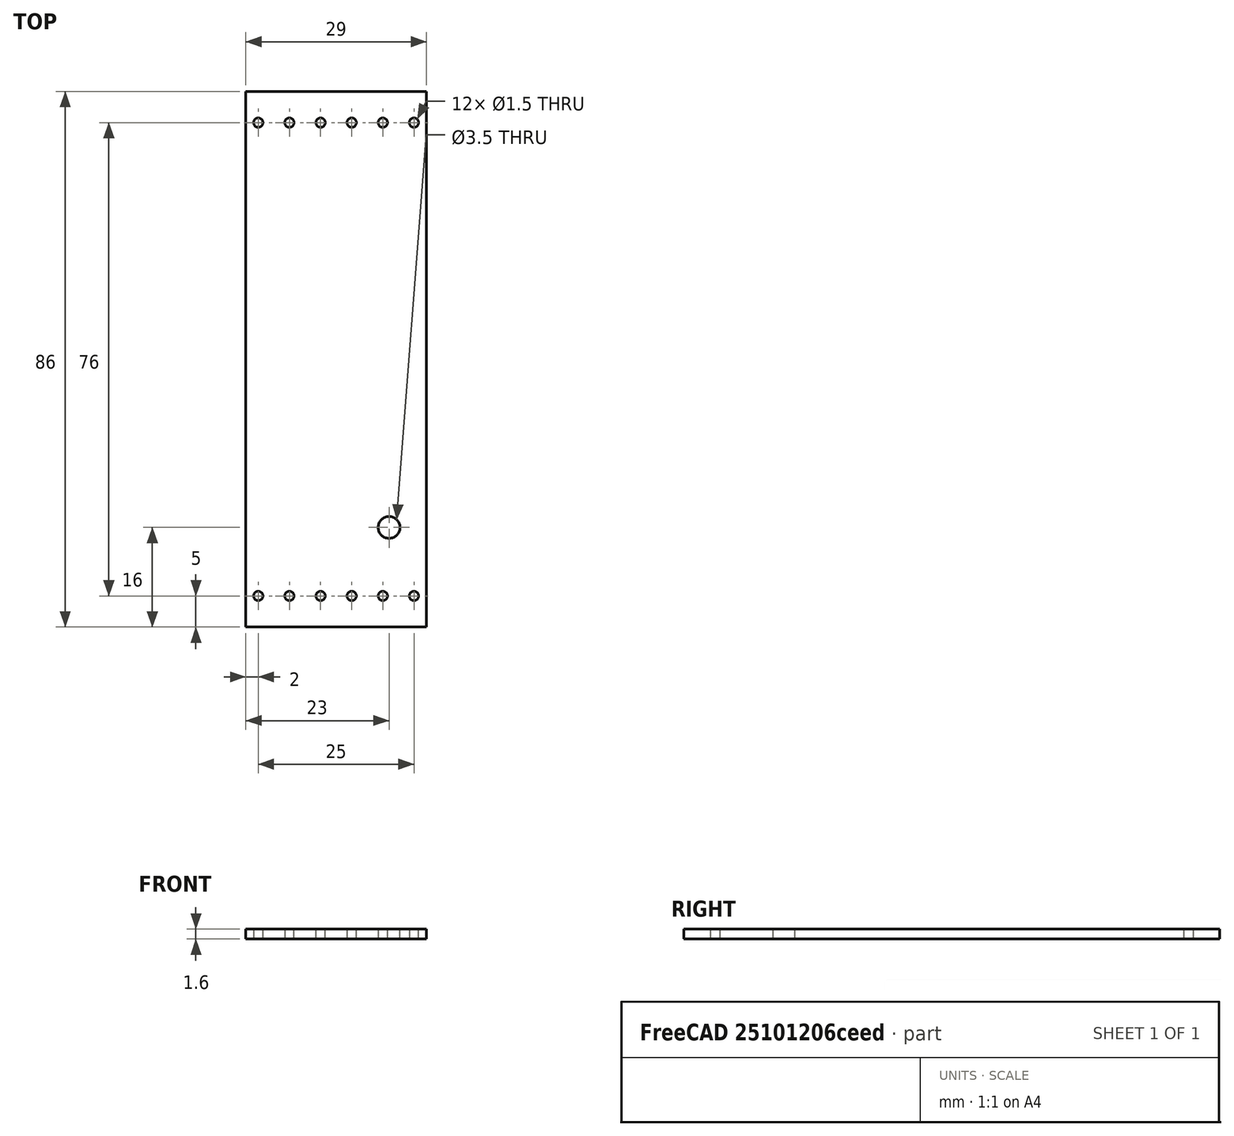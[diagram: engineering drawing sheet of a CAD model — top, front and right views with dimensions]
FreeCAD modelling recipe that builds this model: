
FCSTD DOCUMENT  (FreeCAD 1.0R39319 (Git))
Label: test-pcb-fo-din-holder
License: All rights reserved
LicenseURL: http://en.wikipedia.org/wiki/All_rights_reserved
objects: Sketcher::SketchObject×1, PartDesign::Pad×1, PartDesign::Body×1
note: 6 computed .brp shape members not serialized (recipe doc carries the construction recipe); baked Part::Feature solids carry a one-line shape summary decoded from their .brp

FEATURE [Sketcher::SketchObject] Sketch
  ArcFitTolerance = 1e-06
  AttachmentSupport = -> [XY_Plane001]
  FullyConstrained = true
  MakeInternals = false
  MapMode = 5
  sketch-geometry (19):
    g0: LineSegment StartX=-14.5 StartY=-43 StartZ=0 EndX=14.5 EndY=-43 EndZ=0
    g1: LineSegment StartX=14.5 StartY=-43 StartZ=0 EndX=14.5 EndY=43 EndZ=0
    g2: LineSegment StartX=14.5 StartY=43 StartZ=0 EndX=-14.5 EndY=43 EndZ=0
    g3: LineSegment StartX=-14.5 StartY=43 StartZ=0 EndX=-14.5 EndY=-43 EndZ=0
    g4: GeomPoint [constr] X=0 Y=0 Z=0
    g5: GeomPoint [constr] X=0 Y=0 Z=0
    g6: Circle CenterX=-12.5 CenterY=-38 CenterZ=0 NormalX=0 NormalY=0 NormalZ=1 AngleXU=0 Radius=0.75
    g7: Circle CenterX=-7.5 CenterY=-38 CenterZ=0 NormalX=0 NormalY=0 NormalZ=1 AngleXU=0 Radius=0.75
    g8: Circle CenterX=-2.5 CenterY=-38 CenterZ=0 NormalX=0 NormalY=0 NormalZ=1 AngleXU=0 Radius=0.75
    g9: Circle CenterX=2.5 CenterY=-38 CenterZ=0 NormalX=0 NormalY=0 NormalZ=1 AngleXU=0 Radius=0.75
    g10: Circle CenterX=12.5 CenterY=-38 CenterZ=0 NormalX=0 NormalY=0 NormalZ=1 AngleXU=0 Radius=0.75
    g11: Circle CenterX=7.5 CenterY=-38 CenterZ=0 NormalX=0 NormalY=0 NormalZ=1 AngleXU=0 Radius=0.75
    g12: Circle CenterX=12.5 CenterY=38 CenterZ=0 NormalX=0 NormalY=0 NormalZ=1 AngleXU=0 Radius=0.75
    g13: Circle CenterX=-12.5 CenterY=38 CenterZ=0 NormalX=0 NormalY=0 NormalZ=1 AngleXU=0 Radius=0.75
    g14: Circle CenterX=-7.5 CenterY=38 CenterZ=0 NormalX=0 NormalY=0 NormalZ=1 AngleXU=0 Radius=0.75
    g15: Circle CenterX=-2.5 CenterY=38 CenterZ=0 NormalX=0 NormalY=0 NormalZ=1 AngleXU=0 Radius=0.75
    g16: Circle CenterX=2.5 CenterY=38 CenterZ=0 NormalX=0 NormalY=0 NormalZ=1 AngleXU=0 Radius=0.75
    g17: Circle CenterX=7.5 CenterY=38 CenterZ=0 NormalX=0 NormalY=0 NormalZ=1 AngleXU=0 Radius=0.75
    g18: Circle CenterX=8.5 CenterY=-27 CenterZ=0 NormalX=0 NormalY=0 NormalZ=1 AngleXU=0 Radius=1.75
  constraints (52):
    c: Coincident(g0,g1)
    c: Coincident(g1,g2)
    c: Coincident(g2,g3)
    c: Coincident(g3,g0)
    c: Horizontal(g0)
    c: Horizontal(g2)
    c: Vertical(g1)
    c: Vertical(g3)
    c: Symmetric(g2,g0,g4)
    c: Distance(g1,g3) = 29
    c: Distance(g0,g2) = 86
    c: Coincident(g4,g-1)
    c: Coincident(g5,g4)
    c: Diameter(g6) = 1.5
    c: Distance(g6,g0) = 5
    c: Distance(g6,g3) = 2
    c: Diameter(g7) = 1.5
    c: Distance(g7,g0) = 5
    c: Distance(g7,g6) = 5
    c: Diameter(g8) = 1.5
    c: Diameter(g9) = 1.5
    c: Diameter(g10) = 1.5
    c: Diameter(g11) = 1.5
    c: Distance(g8,g0) = 5
    c: Distance(g8,g7) = 5
    c: Distance(g9,g0) = 5
    c: Distance(g9,g8) = 5
    c: Distance(g11,g0) = 5
    c: Distance(g11,g9) = 5
    c: Distance(g10,g0) = 5
    c: Distance(g10,g11) = 5
    c: Diameter(g12) = 1.5
    c: Diameter(g13) = 1.5
    c: Diameter(g14) = 1.5
    c: Diameter(g15) = 1.5
    c: Diameter(g16) = 1.5
    c: Diameter(g17) = 1.5
    c: Distance(g13,g3) = 2
    c: DistanceX(g13,g14) = 5
    c: DistanceX(g14,g15) = 5
    c: DistanceX(g15,g16) = 5
    c: DistanceX(g16,g17) = 5
    c: DistanceX(g17,g12) = 5
    c: Distance(g13,g2) = 5
    c: Distance(g14,g2) = 5
    c: Distance(g15,g2) = 5
    c: Distance(g16,g2) = 5
    c: Distance(g17,g2) = 5
    c: Distance(g12,g2) = 5
    c: Diameter(g18) = 3.5
    c: Distance(g18,g0) = 16
    c: Distance(g18,g1) = 6
FEATURE [PartDesign::Pad] Pad
  Direction = (0,0,1)
  Length = 1.6
  Length2 = 10
  Profile = -> Sketch
  ReferenceAxis = -> Sketch [N_Axis]
  Refine = true
  Suppressed = false
  Type = 0
FEATURE [PartDesign::Body] Body001
  AllowCompound = false
  Group = -> [Sketch,Pad]
  Origin = -> Origin001
  Tip = -> Pad
